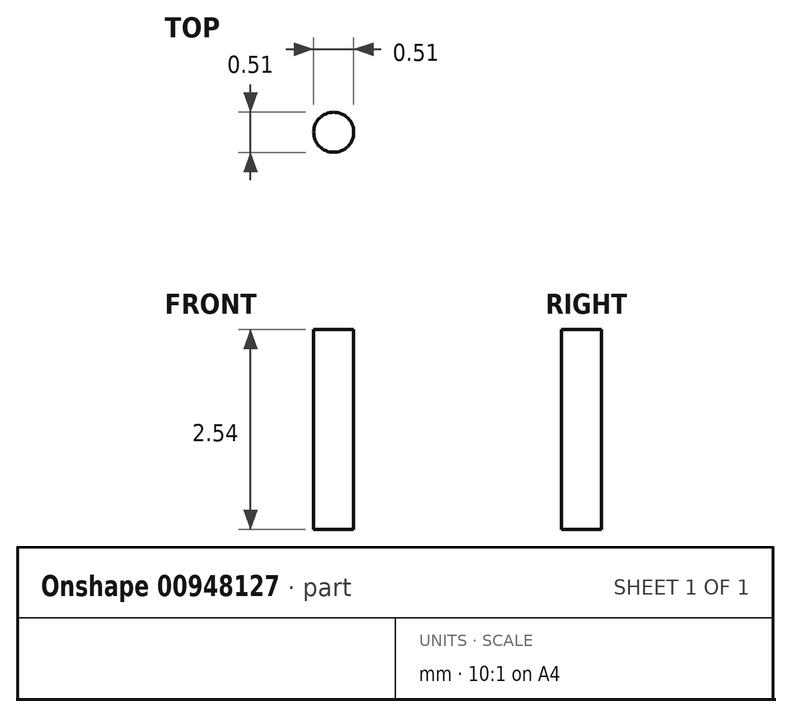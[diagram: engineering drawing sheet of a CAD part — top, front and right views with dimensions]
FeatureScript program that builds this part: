
annotation { "Feature Type Name" : "Feature", "Feature Type Description" : "" }
export const myFeature = defineFeature(function(context is Context, id is Id, definition is map)
    precondition{}
    {
        {
            var Q0;
            Q0=qCreatedBy(makeId("Top.planeOp"),FACE);
            var sketch = newSketch(context, id + "F0", { "sketchPlane" : qUnion([Q0])});
            skCircle(sketch, "E0", {"center": v(-24.31, -14.24) * mm, "radius": 0.25 * mm});
            skSolve(sketch);
        }
        {
            var Q0;
            Q0=makeQuery(id+"F0.imprint","IMPRINT",FACE,{"disambiguationData":[TD([[makeQuery(id+"F0.imprint","IMPRINT",EDGE,{"derivedFrom":sQuery(id+"F0.wireOp",EDGE,"E0")}),1.0]])]});
            extrude(context, id + "F1", {"entities" : qUnion([Q0]), "depth" : 2.54 * mm, "offsetDistance" : 25.4 * mm});
        }
    });
